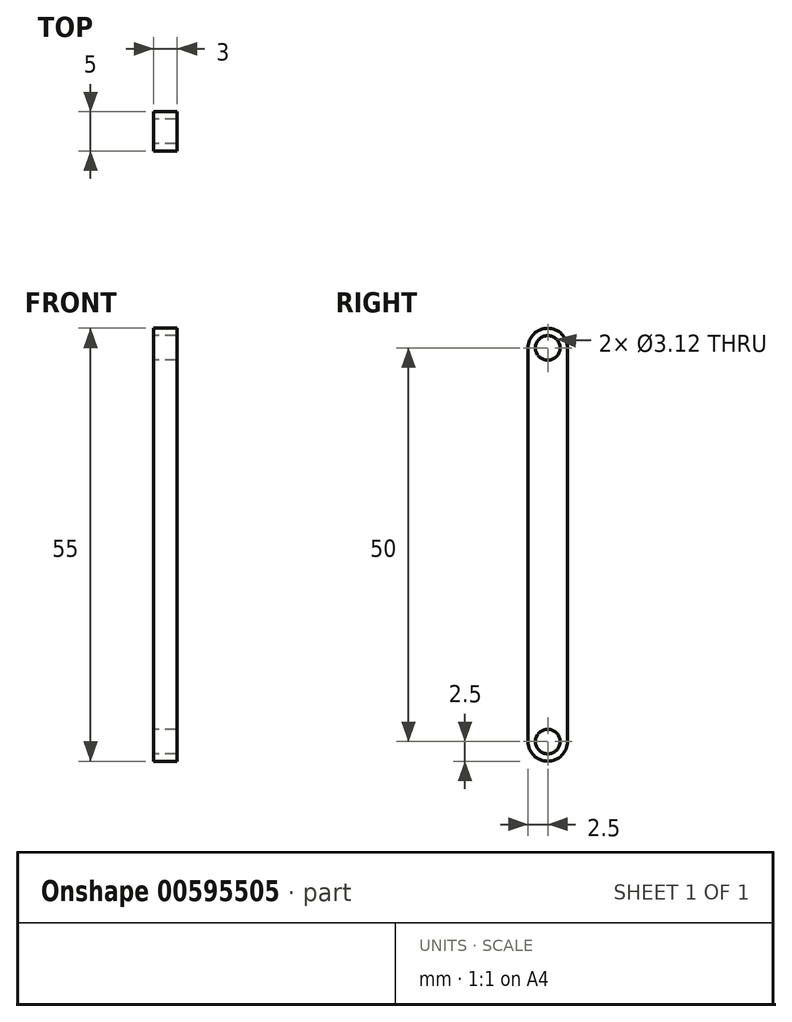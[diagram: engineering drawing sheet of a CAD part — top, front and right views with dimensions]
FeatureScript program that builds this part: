
annotation { "Feature Type Name" : "Feature", "Feature Type Description" : "" }
export const myFeature = defineFeature(function(context is Context, id is Id, definition is map)
    precondition{}
    {
        {
            var Q0;
            Q0=qCreatedBy(makeId("Right.planeOp"),FACE);
            var sketch = newSketch(context, id + "F0", { "sketchPlane" : qUnion([Q0])});
            skLineSegment(sketch, "E0.left", {"start": v(0, 0) * mm, "end": v(0, 50) * mm});
            skLineSegment(sketch, "E0.right", {"start": v(-5, 0) * mm, "end": v(-5, 50) * mm});
            skArc(sketch, "E1", {"start": v(0, 50) * mm, "mid": v(-2.5, 52.5) * mm, "end": v(-5, 50) * mm});
            skArc(sketch, "E2", {"start": v(-5, 0) * mm, "mid": v(-2.5, -2.5) * mm, "end": v(0, 0) * mm});
            skCircle(sketch, "E3", {"center": v(-2.5, 0) * mm, "radius": 1.56 * mm});
            skCircle(sketch, "E4", {"center": v(-2.5, 50) * mm, "radius": 1.56 * mm});
            skSolve(sketch);
        }
        {
            var Q0;
            Q0 = qSketchRegion(id + "F0", true);
            extrude(context, id + "F1", {"entities" : qUnion([Q0]), "depth" : 3 * mm, "offsetDistance" : 25 * mm});
        }
    });
